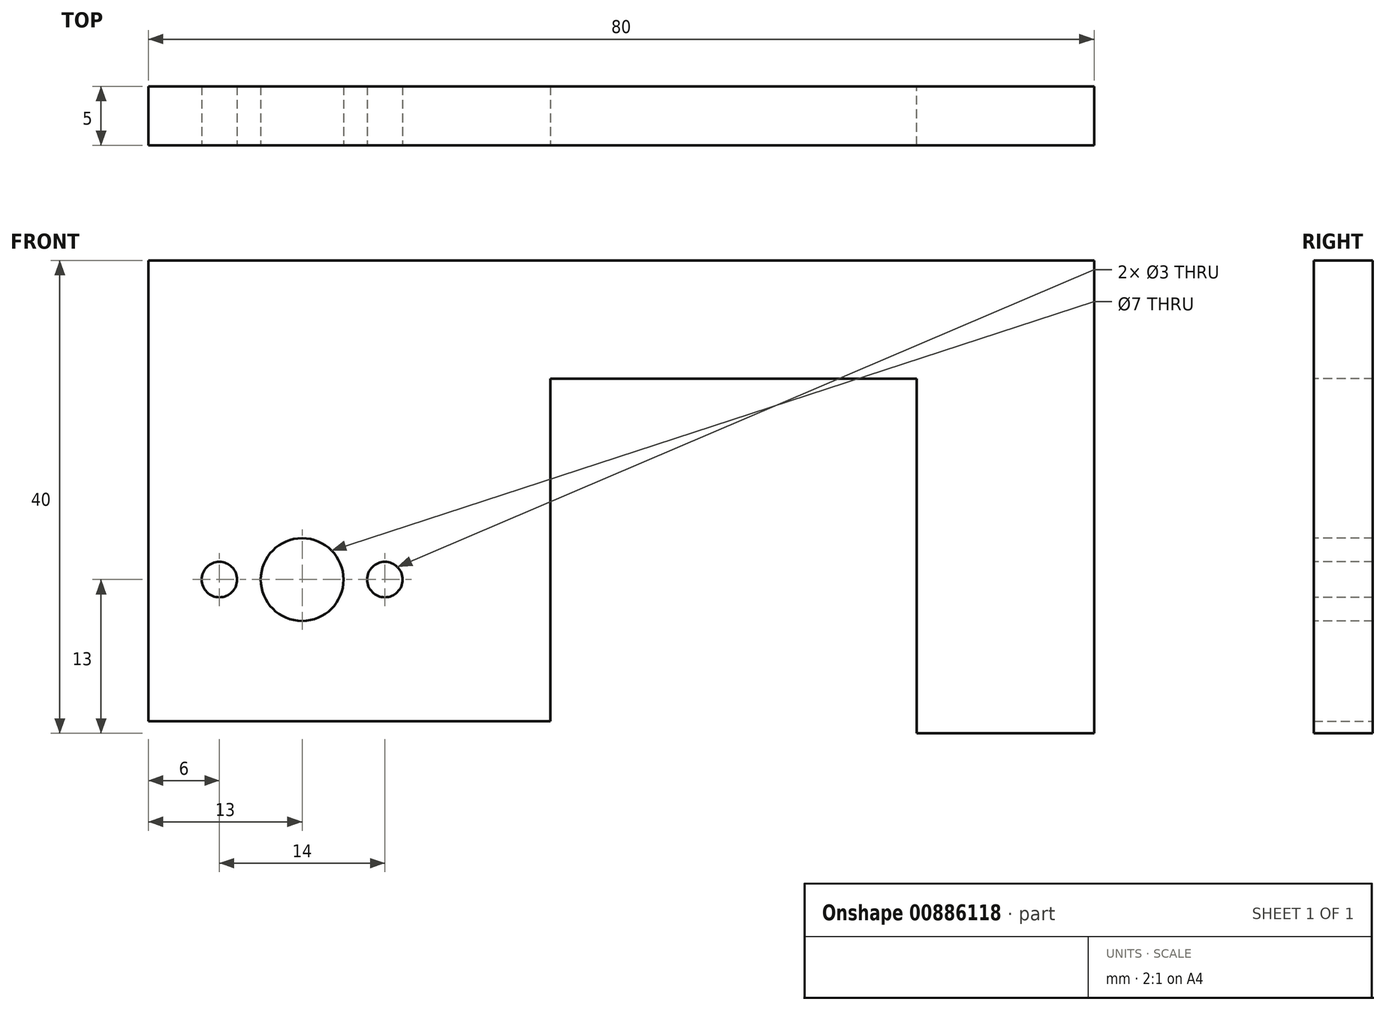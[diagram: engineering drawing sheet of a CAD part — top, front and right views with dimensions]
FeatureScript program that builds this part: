
annotation { "Feature Type Name" : "Feature", "Feature Type Description" : "" }
export const myFeature = defineFeature(function(context is Context, id is Id, definition is map)
    precondition{}
    {
        {
            var Q0;
            Q0=qCreatedBy(makeId("Front.planeOp"),FACE);
            var sketch = newSketch(context, id + "F0", { "sketchPlane" : qUnion([Q0])});
            skLineSegment(sketch, "E0.bottom", {"start": v(-18, 12) * mm, "end": v(18, 12) * mm});
            skLineSegment(sketch, "E0.top", {"start": v(-18, -12) * mm, "end": v(18, -12) * mm});
            skLineSegment(sketch, "E0.left", {"start": v(-18, 12) * mm, "end": v(-18, -12) * mm});
            skLineSegment(sketch, "E0.right", {"start": v(18, 12) * mm, "end": v(18, -12) * mm});
            skPoint(sketch, "E0.middle", {"position": v(0, 0) * mm});
            skSolve(sketch);
        }
        {
            var Q0;
            Q0=qSketchRegion(id+"F0",true);
            extrude(context, id + "F1", {"entities" : qUnion([Q0]), "depth" : 21.5 * mm, "offsetDistance" : 25 * mm});
        }
        {
            var Q0;
            Q0=makeQuery(id+"F1.opExtrude","SWEPT_FACE",FACE,{"disambiguationData":[OSD([sQuery(id+"F0.wireOp",EDGE,"E0.left")])]});
            var sketch = newSketch(context, id + "F2", { "sketchPlane" : qUnion([Q0])});
            skLineSegment(sketch, "E1.bottom", {"start": v(0, 4) * mm, "end": v(-4.5, 4) * mm});
            skLineSegment(sketch, "E1.top", {"start": v(0, -4) * mm, "end": v(-4.5, -4) * mm});
            skLineSegment(sketch, "E1.left", {"start": v(0, 4) * mm, "end": v(0, -4) * mm});
            skLineSegment(sketch, "E1.right", {"start": v(-4.5, 4) * mm, "end": v(-4.5, 1.13) * mm});
            skLineSegment(sketch, "E2.bottom", {"start": v(-3.5, 0.86) * mm, "end": v(-2.3, 0.86) * mm});
            skLineSegment(sketch, "E2.top", {"start": v(-3.5, -0.86) * mm, "end": v(-2.3, -0.86) * mm});
            skLineSegment(sketch, "E2.right", {"start": v(-2.3, 0.86) * mm, "end": v(-2.3, -0.86) * mm});
            skLineSegment(sketch, "E3.trimOffspring", {"start": v(-4.5, -1.13) * mm, "end": v(-4.5, -4) * mm});
            skLineSegment(sketch, "E4", {"start": v(-3.5, -0.86) * mm, "end": v(-4.5, -1.13) * mm});
            skLineSegment(sketch, "E5.MirrorCS", {"start": v(-3.5, 0.86) * mm, "end": v(-4.5, 1.13) * mm});
            skSolve(sketch);
        }
        {
            var Q0;
            Q0=qSketchRegion(id+"F2",true);
            extrude(context, id + "F3", {"entities" : qUnion([Q0]), "operationType" : NewBodyOperationType.ADD, "oppositeDirection" : true, "depth" : 4 * mm, "offsetDistance" : 25 * mm});
        }
        {
            var Q0;
            Q0=makeQuery(id+"F1.opExtrude","CAP_FACE",FACE,{"disambiguationData":[OSD([sQuery(id+"F0.wireOp",EDGE,"E0.bottom"),sQuery(id+"F0.wireOp",EDGE,"E0.top"),sQuery(id+"F0.wireOp",EDGE,"E0.left"),sQuery(id+"F0.wireOp",EDGE,"E0.right")])],"isStart":false});
            var sketch = newSketch(context, id + "F4", { "sketchPlane" : qUnion([Q0])});
            skCircle(sketch, "E6", {"center": v(-12, 0) * mm, "radius": 1.5 * mm});
            skPoint(sketch, "E6.centerSnap0", {"position": v(-18, 0) * mm});
            skCircle(sketch, "E7", {"center": v(2, 0) * mm, "radius": 1.5 * mm});
            skSolve(sketch);
        }
        {
            var Q0;
            Q0=qSketchRegion(id+"F4",true);
            extrude(context, id + "F5", {"entities" : qUnion([Q0]), "operationType" : NewBodyOperationType.REMOVE, "oppositeDirection" : true, "depth" : 6 * mm, "offsetDistance" : 25 * mm});
        }
        {
            var Q0;
            Q0=makeQuery(id+"F1.opExtrude","CAP_FACE",FACE,{"disambiguationData":[OSD([sQuery(id+"F0.wireOp",EDGE,"E0.bottom"),sQuery(id+"F0.wireOp",EDGE,"E0.top"),sQuery(id+"F0.wireOp",EDGE,"E0.left"),sQuery(id+"F0.wireOp",EDGE,"E0.right")])],"isStart":false});
            var sketch = newSketch(context, id + "F6", { "sketchPlane" : qUnion([Q0])});
            skLineSegment(sketch, "E8.bottom", {"start": v(18, 12) * mm, "end": v(16, 12) * mm});
            skLineSegment(sketch, "E8.top", {"start": v(18, -10) * mm, "end": v(16, -10) * mm});
            skLineSegment(sketch, "E8.left", {"start": v(18, 12) * mm, "end": v(18, -10) * mm});
            skLineSegment(sketch, "E8.right", {"start": v(16, 12) * mm, "end": v(16, -10) * mm});
            skCircle(sketch, "E9", {"center": v(-5, 0) * mm, "radius": 1.75 * mm});
            skSolve(sketch);
        }
        {
            var Q0;
            Q0=qSketchRegion(id+"F6",true);
            extrude(context, id + "F7", {"entities" : qUnion([Q0]), "operationType" : NewBodyOperationType.REMOVE, "endBound" : BoundingType.THROUGH_ALL, "oppositeDirection" : true, "depth" : 25 * mm, "offsetDistance" : 25 * mm});
        }
        {
            var Q0;
            Q0=makeQuery(id+"F1.opExtrude","CAP_FACE",FACE,{"disambiguationData":[OSD([sQuery(id+"F0.wireOp",EDGE,"E0.bottom"),sQuery(id+"F0.wireOp",EDGE,"E0.top"),sQuery(id+"F0.wireOp",EDGE,"E0.left"),sQuery(id+"F0.wireOp",EDGE,"E0.right")])],"isStart":false});
            var sketch = newSketch(context, id + "F8", { "sketchPlane" : qUnion([Q0])});
            skCircle(sketch, "E10", {"center": v(-5, 0) * mm, "radius": 3.5 * mm});
            skSolve(sketch);
        }
        {
            var Q0;
            Q0=qSketchRegion(id+"F8",true);
            extrude(context, id + "F9", {"entities" : qUnion([Q0]), "operationType" : NewBodyOperationType.REMOVE, "oppositeDirection" : true, "depth" : 15 * mm, "offsetDistance" : 25 * mm});
        }
        {
            var Q0;
            Q0=makeQuery(id+"F1.opExtrude","SWEPT_FACE",FACE,{"disambiguationData":[OSD([sQuery(id+"F0.wireOp",EDGE,"E0.top")])]});
            var sketch = newSketch(context, id + "F10", { "sketchPlane" : qUnion([Q0])});
            skCircle(sketch, "E11", {"center": v(12, 9.5) * mm, "radius": 1.5 * mm});
            skSolve(sketch);
        }
        {
            var Q0;
            Q0=qSketchRegion(id+"F10",true);
            extrude(context, id + "F11", {"entities" : qUnion([Q0]), "operationType" : NewBodyOperationType.REMOVE, "oppositeDirection" : true, "depth" : 6 * mm, "offsetDistance" : 25 * mm});
        }
        {
            var Q0;
            Q0=makeQuery(id+"F1.opExtrude","CAP_FACE",FACE,{"disambiguationData":[OSD([sQuery(id+"F0.wireOp",EDGE,"E0.bottom"),sQuery(id+"F0.wireOp",EDGE,"E0.top"),sQuery(id+"F0.wireOp",EDGE,"E0.left"),sQuery(id+"F0.wireOp",EDGE,"E0.right")])],"isStart":true});
            var sketch = newSketch(context, id + "F12", { "sketchPlane" : qUnion([Q0])});
            skCircle(sketch, "E12", {"center": v(-12, 0) * mm, "radius": 1.5 * mm});
            skSolve(sketch);
        }
        {
            var Q0;
            Q0=qSketchRegion(id+"F12",true);
            extrude(context, id + "F13", {"entities" : qUnion([Q0]), "operationType" : NewBodyOperationType.REMOVE, "oppositeDirection" : true, "depth" : 6 * mm, "offsetDistance" : 25 * mm});
        }
        {
            var Q0;
            Q0=makeQuery(id+"F1.opExtrude","SWEPT_FACE",FACE,{"disambiguationData":[OSD([sQuery(id+"F0.wireOp",EDGE,"E0.bottom")])]});
            var sketch = newSketch(context, id + "F14", { "sketchPlane" : qUnion([Q0])});
            skLineSegment(sketch, "E13.bottom", {"start": v(-18, -16.5) * mm, "end": v(18, -16.5) * mm});
            skLineSegment(sketch, "E13.left", {"start": v(-18, -16.5) * mm, "end": v(-18, 4.5) * mm});
            skLineSegment(sketch, "E14.0", {"start": v(18, 0) * mm, "end": v(18, -16.5) * mm});
            skLineSegment(sketch, "E15.0", {"start": v(-14, 0) * mm, "end": v(16, 0) * mm});
            skLineSegment(sketch, "E16.0", {"start": v(18, 0) * mm, "end": v(16, 0) * mm});
            skLineSegment(sketch, "E17.0", {"start": v(-14, 4.5) * mm, "end": v(-18, 4.5) * mm});
            skLineSegment(sketch, "E18.0", {"start": v(-14, 0) * mm, "end": v(-14, 4.5) * mm});
            skPoint(sketch, "E19.orphan", {"position": v(-18, 0) * mm});
            skPoint(sketch, "E20.orphan", {"position": v(18, -21.5) * mm});
            skSolve(sketch);
        }
        {
            var Q0;
            Q0 = qSketchRegion(id + "F14", true);
            extrude(context, id + "F15", {"entities" : qUnion([Q0]), "operationType" : NewBodyOperationType.REMOVE, "endBound" : BoundingType.THROUGH_ALL, "oppositeDirection" : true, "depth" : 25 * mm, "offsetDistance" : 25 * mm});
        }
        {
            var Q0;
            Q0=makeQuery(id+"F7.boolean.opBoolean","COPY",FACE,{"derivedFrom":makeQuery(id+"F7.opExtrude","SWEPT_FACE",FACE,{"disambiguationData":[OSD([sQuery(id+"F6.wireOp",EDGE,"E8.top")])]})});
            var sketch = newSketch(context, id + "F16", { "sketchPlane" : qUnion([Q0])});
            skLineSegment(sketch, "E21.bottom", {"start": v(18, -16.5) * mm, "end": v(16, -16.5) * mm});
            skLineSegment(sketch, "E21.top", {"start": v(18, -21.5) * mm, "end": v(16, -21.5) * mm});
            skLineSegment(sketch, "E21.left", {"start": v(18, -16.5) * mm, "end": v(18, -21.5) * mm});
            skLineSegment(sketch, "E21.right", {"start": v(16, -16.5) * mm, "end": v(16, -21.5) * mm});
            skSolve(sketch);
        }
        {
            var Q0;
            Q0 = qSketchRegion(id + "F16", true);
            extrude(context, id + "F17", {"entities" : qUnion([Q0]), "operationType" : NewBodyOperationType.REMOVE, "oppositeDirection" : true, "depth" : 25 * mm, "offsetDistance" : 25 * mm});
        }
        {
            var Q0;
            Q0=makeQuery(id+"F1.opExtrude","SWEPT_FACE",FACE,{"disambiguationData":[OSD([sQuery(id+"F0.wireOp",EDGE,"E0.bottom")])]});
            var sketch = newSketch(context, id + "F18", { "sketchPlane" : qUnion([Q0])});
            skLineSegment(sketch, "E22.0.0", {"start": v(16, -16.5) * mm, "end": v(-18, -16.5) * mm});
            skLineSegment(sketch, "E22.0.1", {"start": v(-18, -16.5) * mm, "end": v(-18, -21.5) * mm});
            skLineSegment(sketch, "E22.0.2", {"start": v(-18, -21.5) * mm, "end": v(16, -21.5) * mm});
            skLineSegment(sketch, "E22.0.3", {"start": v(16, -21.5) * mm, "end": v(16, -16.5) * mm});
            skSolve(sketch);
        }
        {
            var Q0;
            Q0 = qSketchRegion(id + "F18", true);
            extrude(context, id + "F19", {"entities" : qUnion([Q0]), "operationType" : NewBodyOperationType.ADD, "depth" : 25 * mm, "offsetDistance" : 25 * mm});
        }
        {
            var Q0;
            Q0=makeQuery(id+"F19.boolean.opBoolean","MERGE",FACE,{"derivedFrom":[makeQuery(id+"F1.opExtrude","CAP_FACE",FACE,{"disambiguationData":[OSD([sQuery(id+"F0.wireOp",EDGE,"E0.bottom"),sQuery(id+"F0.wireOp",EDGE,"E0.top"),sQuery(id+"F0.wireOp",EDGE,"E0.left"),sQuery(id+"F0.wireOp",EDGE,"E0.right")])],"isStart":false}),makeQuery(id+"F19.opExtrude","SWEPT_FACE",FACE,{"disambiguationData":[OSD([sQuery(id+"F18.wireOp",EDGE,"E22.0.2")])]})]});
            var sketch = newSketch(context, id + "F20", { "sketchPlane" : qUnion([Q0])});
            skLineSegment(sketch, "E23.bottom", {"start": v(-18, 37) * mm, "end": v(62, 37) * mm});
            skLineSegment(sketch, "E23.top", {"start": v(-18, 17) * mm, "end": v(62, 17) * mm});
            skLineSegment(sketch, "E23.left", {"start": v(-18, 37) * mm, "end": v(-18, 17) * mm});
            skLineSegment(sketch, "E23.right", {"start": v(62, 37) * mm, "end": v(62, 17) * mm});
            skSolve(sketch);
        }
        {
            var Q0;
            Q0 = qSketchRegion(id + "F20", true);
            extrude(context, id + "F21", {"entities" : qUnion([Q0]), "operationType" : NewBodyOperationType.ADD, "oppositeDirection" : true, "depth" : 5 * mm, "offsetDistance" : 25 * mm});
        }
        {
            var Q0;
            Q0=makeQuery(id+"F21.opExtrude","SWEPT_FACE",FACE,{"disambiguationData":[OSD([sQuery(id+"F20.wireOp",EDGE,"E23.top")])]});
            var sketch = newSketch(context, id + "F22", { "sketchPlane" : qUnion([Q0])});
            skLineSegment(sketch, "E24.bottom", {"start": v(62, 21.5) * mm, "end": v(47, 21.5) * mm});
            skLineSegment(sketch, "E24.top", {"start": v(62, 16.5) * mm, "end": v(47, 16.5) * mm});
            skLineSegment(sketch, "E24.left", {"start": v(62, 21.5) * mm, "end": v(62, 16.5) * mm});
            skLineSegment(sketch, "E24.right", {"start": v(47, 21.5) * mm, "end": v(47, 16.5) * mm});
            skSolve(sketch);
        }
        {
            var Q0;
            Q0 = qSketchRegion(id + "F22", true);
            extrude(context, id + "F23", {"entities" : qUnion([Q0]), "operationType" : NewBodyOperationType.ADD, "depth" : 30 * mm, "offsetDistance" : 25 * mm});
        }
        {
            var Q0;
            Q0=makeQuery(id+"F23.boolean.opBoolean","MERGE",FACE,{"derivedFrom":[makeQuery(id+"F21.boolean.opBoolean","MERGE",FACE,{"derivedFrom":[makeQuery(id+"F19.boolean.opBoolean","MERGE",FACE,{"derivedFrom":[makeQuery(id+"F1.opExtrude","CAP_FACE",FACE,{"disambiguationData":[OSD([sQuery(id+"F0.wireOp",EDGE,"E0.bottom"),sQuery(id+"F0.wireOp",EDGE,"E0.top"),sQuery(id+"F0.wireOp",EDGE,"E0.left"),sQuery(id+"F0.wireOp",EDGE,"E0.right")])],"isStart":false}),makeQuery(id+"F19.opExtrude","SWEPT_FACE",FACE,{"disambiguationData":[OSD([sQuery(id+"F18.wireOp",EDGE,"E22.0.2")])]})]}),makeQuery(id+"F21.opExtrude","CAP_FACE",FACE,{"disambiguationData":[OSD([sQuery(id+"F20.wireOp",EDGE,"E23.bottom"),sQuery(id+"F20.wireOp",EDGE,"E23.top"),sQuery(id+"F20.wireOp",EDGE,"E23.left"),sQuery(id+"F20.wireOp",EDGE,"E23.right")])],"isStart":true})]}),makeQuery(id+"F23.opExtrude","SWEPT_FACE",FACE,{"disambiguationData":[OSD([sQuery(id+"F22.wireOp",EDGE,"E24.bottom")])]})]});
            var sketch = newSketch(context, id + "F24", { "sketchPlane" : qUnion([Q0])});
            skLineSegment(sketch, "E25.bottom", {"start": v(62, 37) * mm, "end": v(-18, 37) * mm});
            skLineSegment(sketch, "E25.top", {"start": v(62, 27) * mm, "end": v(-18, 27) * mm});
            skLineSegment(sketch, "E25.left", {"start": v(62, 37) * mm, "end": v(62, 27) * mm});
            skLineSegment(sketch, "E25.right", {"start": v(-18, 37) * mm, "end": v(-18, 27) * mm});
            skSolve(sketch);
        }
        {
            var Q0;
            Q0 = qSketchRegion(id + "F24", true);
            extrude(context, id + "F25", {"entities" : qUnion([Q0]), "operationType" : NewBodyOperationType.REMOVE, "endBound" : BoundingType.THROUGH_ALL, "oppositeDirection" : true, "depth" : 25 * mm, "offsetDistance" : 25 * mm});
        }
    });
